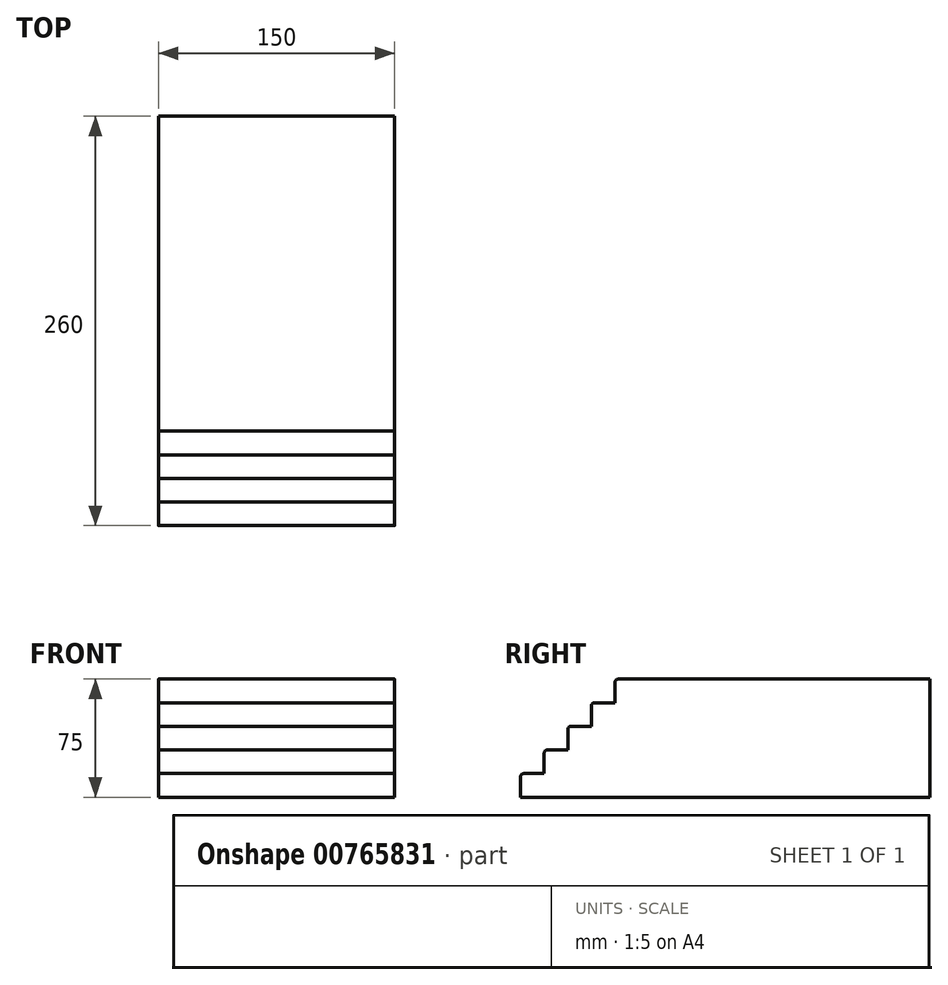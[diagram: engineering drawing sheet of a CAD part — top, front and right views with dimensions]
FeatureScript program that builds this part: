
annotation { "Feature Type Name" : "Feature", "Feature Type Description" : "" }
export const myFeature = defineFeature(function(context is Context, id is Id, definition is map)
    precondition{}
    {
        {
            var Q0;
            Q0=qCreatedBy(makeId("Right.planeOp"),FACE);
            var sketch = newSketch(context, id + "F0", { "sketchPlane" : qUnion([Q0])});
            skLineSegment(sketch, "E0", {"start": v(0, 0) * mm, "end": v(200, 0) * mm});
            skLineSegment(sketch, "E1", {"start": v(200, 0) * mm, "end": v(200, -75) * mm});
            skLineSegment(sketch, "E2", {"start": v(0, 0) * mm, "end": v(0, -15) * mm});
            skLineSegment(sketch, "E3", {"start": v(0, -15) * mm, "end": v(-15, -15) * mm});
            skLineSegment(sketch, "E4", {"start": v(-15, -15) * mm, "end": v(-15, -30) * mm});
            skLineSegment(sketch, "E5", {"start": v(-15, -30) * mm, "end": v(-30, -30) * mm});
            skLineSegment(sketch, "E6", {"start": v(-30, -30) * mm, "end": v(-30, -45) * mm});
            skLineSegment(sketch, "E7", {"start": v(-30, -45) * mm, "end": v(-45, -45) * mm});
            skLineSegment(sketch, "E8", {"start": v(-45, -45) * mm, "end": v(-45, -60) * mm});
            skLineSegment(sketch, "E9", {"start": v(-45, -60) * mm, "end": v(-60, -60) * mm});
            skLineSegment(sketch, "E10", {"start": v(-60, -60) * mm, "end": v(-60, -75) * mm});
            skLineSegment(sketch, "E11", {"start": v(-60, -75) * mm, "end": v(200, -75) * mm});
            skSolve(sketch);
        }
        {
            var Q0;
            Q0 = qSketchRegion(id + "F0", true);
            extrude(context, id + "F1", {"entities" : qUnion([Q0]), "depth" : 150 * mm, "offsetDistance" : 25 * mm});
        }
        {
            var Q0;
            Q0=makeQuery(id+"F1.opExtrude","SWEPT_EDGE",EDGE,{"disambiguationData":[OSD([sQuery(id+"F0.wireOp",EDGE,"E3"),sQuery(id+"F0.wireOp",EDGE,"E4")])]});
            var Q1;
            Q1=makeQuery(id+"F1.opExtrude","SWEPT_EDGE",EDGE,{"disambiguationData":[OSD([sQuery(id+"F0.wireOp",EDGE,"E0"),sQuery(id+"F0.wireOp",EDGE,"E2")])]});
            var Q2;
            Q2=makeQuery(id+"F1.opExtrude","SWEPT_EDGE",EDGE,{"disambiguationData":[OSD([sQuery(id+"F0.wireOp",EDGE,"E5"),sQuery(id+"F0.wireOp",EDGE,"E6")])]});
            var Q3;
            Q3=makeQuery(id+"F1.opExtrude","SWEPT_EDGE",EDGE,{"disambiguationData":[OSD([sQuery(id+"F0.wireOp",EDGE,"E7"),sQuery(id+"F0.wireOp",EDGE,"E8")])]});
            var Q4;
            Q4=makeQuery(id+"F1.opExtrude","SWEPT_EDGE",EDGE,{"disambiguationData":[OSD([sQuery(id+"F0.wireOp",EDGE,"E9"),sQuery(id+"F0.wireOp",EDGE,"E10")])]});
            fillet(context, id + "F2", {"entities" : qUnion([Q0, Q1, Q2, Q3, Q4]), "radius" : 2 * mm, "tangentPropagation" : true, "allowEdgeOverflow" : false});
        }
    });
